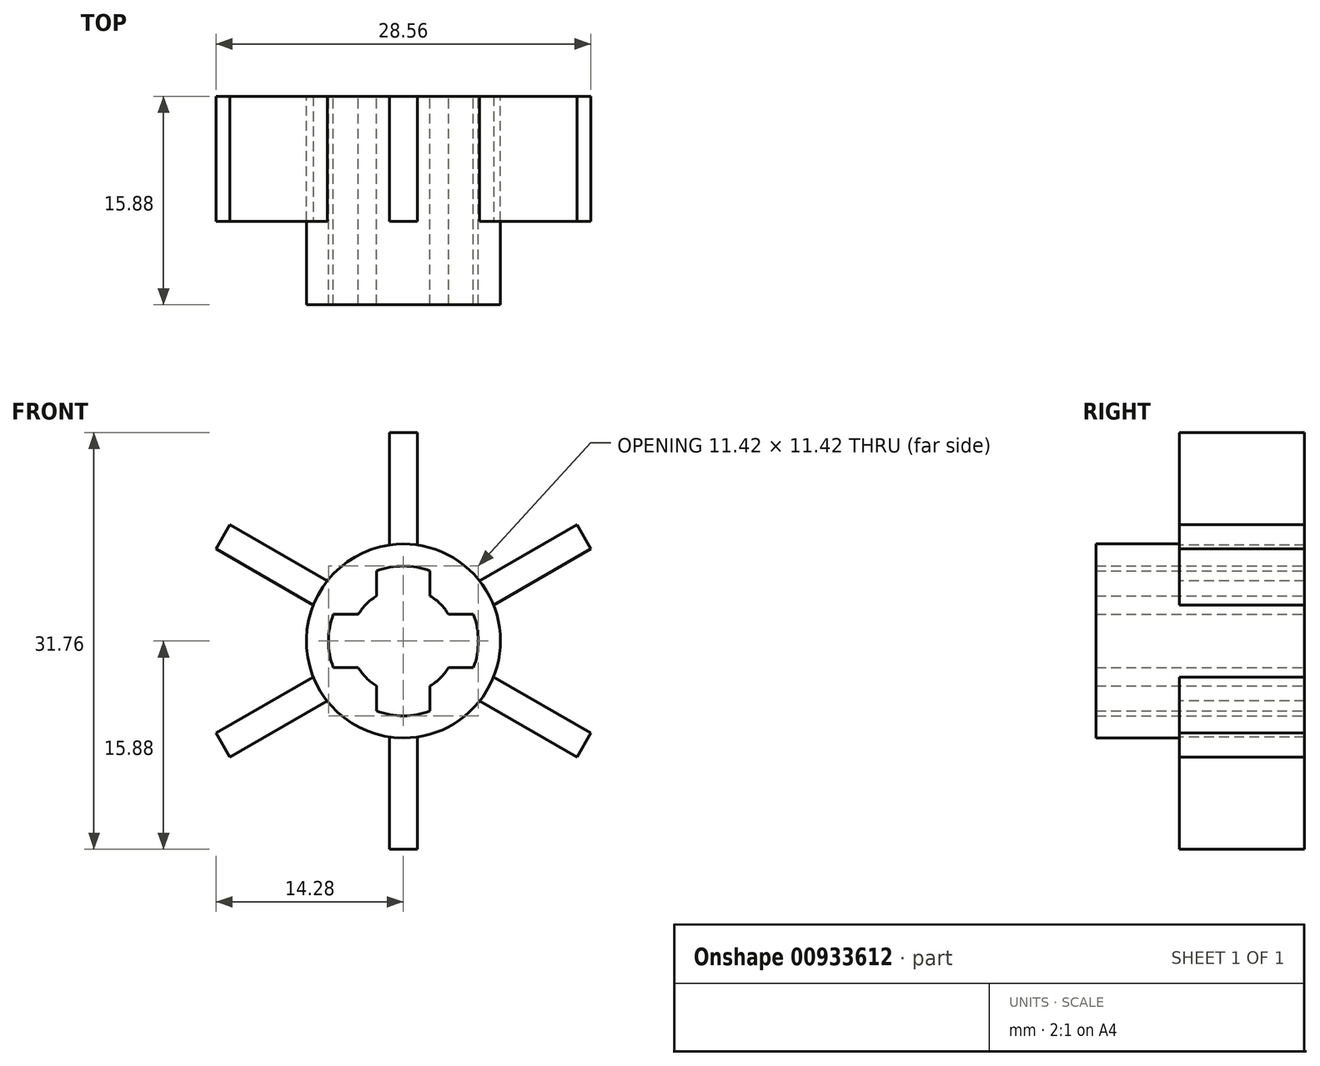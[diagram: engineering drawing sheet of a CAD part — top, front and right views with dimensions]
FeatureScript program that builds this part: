
annotation { "Feature Type Name" : "Feature", "Feature Type Description" : "" }
export const myFeature = defineFeature(function(context is Context, id is Id, definition is map)
    precondition{}
    {
        {
            var Q0;
            Q0=qCreatedBy(makeId("Front.planeOp"),FACE);
            var sketch = newSketch(context, id + "F0", { "sketchPlane" : qUnion([Q0])});
            skArc(sketch, "E0", {"start": v(-1.05, 6.26) * mm, "mid": v(-3.18, 5.5) * mm, "end": v(-4.9, 4.04) * mm});
            skCircle(sketch, "E1", {"center": v(0, 0) * mm, "radius": 3.99 * mm});
            skLineSegment(sketch, "E2.bottom", {"start": v(-1.05, 15.88) * mm, "end": v(1.05, 15.88) * mm});
            skLineSegment(sketch, "E2.top", {"start": v(-1.05, 6.26) * mm, "end": v(1.05, 6.26) * mm, "construction": true});
            skLineSegment(sketch, "E2.left", {"start": v(-1.05, 15.88) * mm, "end": v(-1.05, 6.26) * mm});
            skLineSegment(sketch, "E2.right", {"start": v(1.05, 15.88) * mm, "end": v(1.05, 6.26) * mm});
            skLineSegment(sketch, "E3", {"start": v(0, 0) * mm, "end": v(0, 6.26) * mm, "construction": true});
            skLineSegment(sketch, "E4", {"start": v(0, 0) * mm, "end": v(9.86, 0) * mm, "construction": true});
            skLineSegment(sketch, "E5.1.0", {"start": v(0, 0) * mm, "end": v(-5.42, 3.13) * mm, "construction": true});
            skLineSegment(sketch, "E5.1.1", {"start": v(-13.22, 8.85) * mm, "end": v(-4.9, 4.04) * mm});
            skLineSegment(sketch, "E5.1.2", {"start": v(-14.28, 7.02) * mm, "end": v(-13.22, 8.85) * mm});
            skLineSegment(sketch, "E5.1.3", {"start": v(-14.28, 7.02) * mm, "end": v(-5.95, 2.22) * mm});
            skLineSegment(sketch, "E5.2.0", {"start": v(0, 0) * mm, "end": v(-5.42, -3.13) * mm, "construction": true});
            skLineSegment(sketch, "E5.2.1", {"start": v(-14.28, -7.02) * mm, "end": v(-5.95, -2.22) * mm});
            skLineSegment(sketch, "E5.2.2", {"start": v(-13.22, -8.85) * mm, "end": v(-14.28, -7.02) * mm});
            skLineSegment(sketch, "E5.2.3", {"start": v(-13.22, -8.85) * mm, "end": v(-4.9, -4.04) * mm});
            skLineSegment(sketch, "E5.3.0", {"start": v(0, 0) * mm, "end": v(0, -6.26) * mm, "construction": true});
            skLineSegment(sketch, "E5.3.1", {"start": v(-1.05, -15.88) * mm, "end": v(-1.05, -6.26) * mm});
            skLineSegment(sketch, "E5.3.2", {"start": v(1.05, -15.88) * mm, "end": v(-1.05, -15.88) * mm});
            skLineSegment(sketch, "E5.3.3", {"start": v(1.05, -15.88) * mm, "end": v(1.05, -6.26) * mm});
            skLineSegment(sketch, "E5.4.0", {"start": v(0, 0) * mm, "end": v(5.42, -3.13) * mm, "construction": true});
            skLineSegment(sketch, "E5.4.1", {"start": v(13.22, -8.85) * mm, "end": v(4.9, -4.04) * mm});
            skLineSegment(sketch, "E5.4.2", {"start": v(14.28, -7.02) * mm, "end": v(13.22, -8.85) * mm});
            skLineSegment(sketch, "E5.4.3", {"start": v(14.28, -7.02) * mm, "end": v(5.95, -2.22) * mm});
            skLineSegment(sketch, "E5.5.0", {"start": v(0, 0) * mm, "end": v(5.42, 3.13) * mm, "construction": true});
            skLineSegment(sketch, "E5.5.1", {"start": v(14.28, 7.02) * mm, "end": v(5.95, 2.22) * mm});
            skLineSegment(sketch, "E5.5.2", {"start": v(13.22, 8.85) * mm, "end": v(14.28, 7.02) * mm});
            skLineSegment(sketch, "E5.5.3", {"start": v(13.22, 8.85) * mm, "end": v(4.9, 4.04) * mm});
            skArc(sketch, "E6.trimOffspring", {"start": v(4.9, 4.04) * mm, "mid": v(3.17, 5.5) * mm, "end": v(1.05, 6.26) * mm});
            skArc(sketch, "E7.trimOffspring", {"start": v(5.95, -2.22) * mm, "mid": v(6.35, 0) * mm, "end": v(5.95, 2.22) * mm});
            skArc(sketch, "E8.trimOffspring", {"start": v(1.05, -6.26) * mm, "mid": v(3.17, -5.5) * mm, "end": v(4.9, -4.04) * mm});
            skArc(sketch, "E9.trimOffspring", {"start": v(-4.9, -4.04) * mm, "mid": v(-3.18, -5.5) * mm, "end": v(-1.05, -6.26) * mm});
            skArc(sketch, "E10.trimOffspring", {"start": v(-5.95, 2.22) * mm, "mid": v(-6.35, 0) * mm, "end": v(-5.95, -2.22) * mm});
            skSolve(sketch);
        }
        {
            var Q0;
            Q0 = qSketchRegion(id + "F0", true);
            extrude(context, id + "F1", {"entities" : qUnion([Q0]), "depth" : 9.52 * mm, "offsetDistance" : 25.4 * mm});
        }
        {
            var Q0;
            Q0=makeQuery(id+"F1.opExtrude","CAP_FACE",FACE,{"disambiguationData":[OSD([sQuery(id+"F0.wireOp",EDGE,"E0"),sQuery(id+"F0.wireOp",EDGE,"E1"),sQuery(id+"F0.wireOp",EDGE,"E2.bottom"),sQuery(id+"F0.wireOp",EDGE,"E2.left"),sQuery(id+"F0.wireOp",EDGE,"E2.right"),sQuery(id+"F0.wireOp",EDGE,"E5.1.1"),sQuery(id+"F0.wireOp",EDGE,"E5.1.2"),sQuery(id+"F0.wireOp",EDGE,"E5.1.3"),sQuery(id+"F0.wireOp",EDGE,"E5.2.1"),sQuery(id+"F0.wireOp",EDGE,"E5.2.2"),sQuery(id+"F0.wireOp",EDGE,"E5.2.3"),sQuery(id+"F0.wireOp",EDGE,"E5.3.1"),sQuery(id+"F0.wireOp",EDGE,"E5.3.2"),sQuery(id+"F0.wireOp",EDGE,"E5.3.3"),sQuery(id+"F0.wireOp",EDGE,"E5.4.1"),sQuery(id+"F0.wireOp",EDGE,"E5.4.2"),sQuery(id+"F0.wireOp",EDGE,"E5.4.3"),sQuery(id+"F0.wireOp",EDGE,"E5.5.1"),sQuery(id+"F0.wireOp",EDGE,"E5.5.2"),sQuery(id+"F0.wireOp",EDGE,"E5.5.3"),sQuery(id+"F0.wireOp",EDGE,"E6.trimOffspring"),sQuery(id+"F0.wireOp",EDGE,"E7.trimOffspring"),sQuery(id+"F0.wireOp",EDGE,"E8.trimOffspring"),sQuery(id+"F0.wireOp",EDGE,"E9.trimOffspring"),sQuery(id+"F0.wireOp",EDGE,"E10.trimOffspring")])],"isStart":false});
            var sketch = newSketch(context, id + "F2", { "sketchPlane" : qUnion([Q0])});
            skCircle(sketch, "E11", {"center": v(0, 0) * mm, "radius": 7.4 * mm});
            skArc(sketch, "E12", {"start": v(-2.03, 3.43) * mm, "mid": v(-2.82, 2.82) * mm, "end": v(-3.43, 2.03) * mm});
            skLineSegment(sketch, "E13.bottom", {"start": v(-2.03, 5.33) * mm, "end": v(2.03, 5.33) * mm, "construction": true});
            skLineSegment(sketch, "E13.top", {"start": v(-2.03, 3.43) * mm, "end": v(2.03, 3.43) * mm, "construction": true});
            skLineSegment(sketch, "E13.left", {"start": v(-2.03, 5.33) * mm, "end": v(-2.03, 3.43) * mm});
            skLineSegment(sketch, "E13.right", {"start": v(2.03, 5.33) * mm, "end": v(2.03, 3.43) * mm});
            skLineSegment(sketch, "E14", {"start": v(0, 0) * mm, "end": v(0, 3.43) * mm, "construction": true});
            skPoint(sketch, "E14.endSnap0", {"position": v(0, 3.43) * mm});
            skLineSegment(sketch, "E15", {"start": v(0, 0) * mm, "end": v(1.34, 0) * mm, "construction": true});
            skArc(sketch, "E16", {"start": v(2.03, 5.33) * mm, "mid": v(0, 5.7) * mm, "end": v(-2.03, 5.33) * mm});
            skLineSegment(sketch, "E17.1.0", {"start": v(0, 0) * mm, "end": v(-3.43, 0) * mm, "construction": true});
            skLineSegment(sketch, "E17.1.1", {"start": v(-5.33, -2.03) * mm, "end": v(-3.43, -2.03) * mm});
            skArc(sketch, "E17.1.2", {"start": v(-5.33, 2.03) * mm, "mid": v(-5.7, 0) * mm, "end": v(-5.33, -2.03) * mm});
            skLineSegment(sketch, "E17.1.3", {"start": v(-5.33, 2.03) * mm, "end": v(-3.43, 2.03) * mm});
            skLineSegment(sketch, "E17.2.0", {"start": v(0, 0) * mm, "end": v(0, -3.43) * mm, "construction": true});
            skLineSegment(sketch, "E17.2.1", {"start": v(2.03, -5.33) * mm, "end": v(2.03, -3.43) * mm});
            skArc(sketch, "E17.2.2", {"start": v(-2.03, -5.33) * mm, "mid": v(0, -5.7) * mm, "end": v(2.03, -5.33) * mm});
            skLineSegment(sketch, "E17.2.3", {"start": v(-2.03, -5.33) * mm, "end": v(-2.03, -3.43) * mm});
            skLineSegment(sketch, "E17.3.0", {"start": v(0, 0) * mm, "end": v(3.43, 0) * mm, "construction": true});
            skLineSegment(sketch, "E17.3.1", {"start": v(5.33, 2.03) * mm, "end": v(3.43, 2.03) * mm});
            skArc(sketch, "E17.3.2", {"start": v(5.33, -2.03) * mm, "mid": v(5.7, 0) * mm, "end": v(5.33, 2.03) * mm});
            skLineSegment(sketch, "E17.3.3", {"start": v(5.33, -2.03) * mm, "end": v(3.43, -2.03) * mm});
            skArc(sketch, "E18.trimOffspring", {"start": v(-3.43, -2.03) * mm, "mid": v(-2.82, -2.82) * mm, "end": v(-2.03, -3.43) * mm});
            skArc(sketch, "E19.trimOffspring", {"start": v(3.43, 2.03) * mm, "mid": v(2.82, 2.82) * mm, "end": v(2.03, 3.43) * mm});
            skArc(sketch, "E20.trimOffspring", {"start": v(2.03, -3.43) * mm, "mid": v(2.82, -2.82) * mm, "end": v(3.43, -2.03) * mm});
            skSolve(sketch);
        }
        {
            var Q0;
            Q0 = qSketchRegion(id + "F2", true);
            extrude(context, id + "F3", {"entities" : qUnion([Q0]), "operationType" : NewBodyOperationType.ADD, "depth" : 6.35 * mm, "offsetDistance" : 25.4 * mm});
        }
        {
            var Q0;
            {var subQ0=sQuery(id+"F0.wireOp",EDGE,"E1");Q0=makeQuery(id+"F3.boolean.opBoolean","SPLIT",FACE,{"disambiguationData":[TD([makeQuery(id+"F3.opExtrude","SWEPT_FACE",FACE,{"disambiguationData":[OSD([sQuery(id+"F2.wireOp",EDGE,"E17.3.1")])]})])],"derivedFrom":makeQuery(id+"F1.opExtrude","CAP_FACE",FACE,{"disambiguationData":[OSD([sQuery(id+"F0.wireOp",EDGE,"E0"),subQ0,sQuery(id+"F0.wireOp",EDGE,"E2.bottom"),sQuery(id+"F0.wireOp",EDGE,"E2.left"),sQuery(id+"F0.wireOp",EDGE,"E2.right"),sQuery(id+"F0.wireOp",EDGE,"E5.1.1"),sQuery(id+"F0.wireOp",EDGE,"E5.1.2"),sQuery(id+"F0.wireOp",EDGE,"E5.1.3"),sQuery(id+"F0.wireOp",EDGE,"E5.2.1"),sQuery(id+"F0.wireOp",EDGE,"E5.2.2"),sQuery(id+"F0.wireOp",EDGE,"E5.2.3"),sQuery(id+"F0.wireOp",EDGE,"E5.3.1"),sQuery(id+"F0.wireOp",EDGE,"E5.3.2"),sQuery(id+"F0.wireOp",EDGE,"E5.3.3"),sQuery(id+"F0.wireOp",EDGE,"E5.4.1"),sQuery(id+"F0.wireOp",EDGE,"E5.4.2"),sQuery(id+"F0.wireOp",EDGE,"E5.4.3"),sQuery(id+"F0.wireOp",EDGE,"E5.5.1"),sQuery(id+"F0.wireOp",EDGE,"E5.5.2"),sQuery(id+"F0.wireOp",EDGE,"E5.5.3"),sQuery(id+"F0.wireOp",EDGE,"E6.trimOffspring"),sQuery(id+"F0.wireOp",EDGE,"E7.trimOffspring"),sQuery(id+"F0.wireOp",EDGE,"E8.trimOffspring"),sQuery(id+"F0.wireOp",EDGE,"E9.trimOffspring"),sQuery(id+"F0.wireOp",EDGE,"E10.trimOffspring")])],"isStart":false})});}
            var Q1;
            {var subQ0=sQuery(id+"F0.wireOp",EDGE,"E1");Q1=makeQuery(id+"F3.boolean.opBoolean","SPLIT",FACE,{"disambiguationData":[TD([makeQuery(id+"F3.opExtrude","SWEPT_FACE",FACE,{"disambiguationData":[OSD([sQuery(id+"F2.wireOp",EDGE,"E17.2.1")])]})])],"derivedFrom":makeQuery(id+"F1.opExtrude","CAP_FACE",FACE,{"disambiguationData":[OSD([sQuery(id+"F0.wireOp",EDGE,"E0"),subQ0,sQuery(id+"F0.wireOp",EDGE,"E2.bottom"),sQuery(id+"F0.wireOp",EDGE,"E2.left"),sQuery(id+"F0.wireOp",EDGE,"E2.right"),sQuery(id+"F0.wireOp",EDGE,"E5.1.1"),sQuery(id+"F0.wireOp",EDGE,"E5.1.2"),sQuery(id+"F0.wireOp",EDGE,"E5.1.3"),sQuery(id+"F0.wireOp",EDGE,"E5.2.1"),sQuery(id+"F0.wireOp",EDGE,"E5.2.2"),sQuery(id+"F0.wireOp",EDGE,"E5.2.3"),sQuery(id+"F0.wireOp",EDGE,"E5.3.1"),sQuery(id+"F0.wireOp",EDGE,"E5.3.2"),sQuery(id+"F0.wireOp",EDGE,"E5.3.3"),sQuery(id+"F0.wireOp",EDGE,"E5.4.1"),sQuery(id+"F0.wireOp",EDGE,"E5.4.2"),sQuery(id+"F0.wireOp",EDGE,"E5.4.3"),sQuery(id+"F0.wireOp",EDGE,"E5.5.1"),sQuery(id+"F0.wireOp",EDGE,"E5.5.2"),sQuery(id+"F0.wireOp",EDGE,"E5.5.3"),sQuery(id+"F0.wireOp",EDGE,"E6.trimOffspring"),sQuery(id+"F0.wireOp",EDGE,"E7.trimOffspring"),sQuery(id+"F0.wireOp",EDGE,"E8.trimOffspring"),sQuery(id+"F0.wireOp",EDGE,"E9.trimOffspring"),sQuery(id+"F0.wireOp",EDGE,"E10.trimOffspring")])],"isStart":false})});}
            var Q2;
            {var subQ0=sQuery(id+"F0.wireOp",EDGE,"E1");Q2=makeQuery(id+"F3.boolean.opBoolean","SPLIT",FACE,{"disambiguationData":[TD([makeQuery(id+"F3.opExtrude","SWEPT_FACE",FACE,{"disambiguationData":[OSD([sQuery(id+"F2.wireOp",EDGE,"E13.left")])]})])],"derivedFrom":makeQuery(id+"F1.opExtrude","CAP_FACE",FACE,{"disambiguationData":[OSD([sQuery(id+"F0.wireOp",EDGE,"E0"),subQ0,sQuery(id+"F0.wireOp",EDGE,"E2.bottom"),sQuery(id+"F0.wireOp",EDGE,"E2.left"),sQuery(id+"F0.wireOp",EDGE,"E2.right"),sQuery(id+"F0.wireOp",EDGE,"E5.1.1"),sQuery(id+"F0.wireOp",EDGE,"E5.1.2"),sQuery(id+"F0.wireOp",EDGE,"E5.1.3"),sQuery(id+"F0.wireOp",EDGE,"E5.2.1"),sQuery(id+"F0.wireOp",EDGE,"E5.2.2"),sQuery(id+"F0.wireOp",EDGE,"E5.2.3"),sQuery(id+"F0.wireOp",EDGE,"E5.3.1"),sQuery(id+"F0.wireOp",EDGE,"E5.3.2"),sQuery(id+"F0.wireOp",EDGE,"E5.3.3"),sQuery(id+"F0.wireOp",EDGE,"E5.4.1"),sQuery(id+"F0.wireOp",EDGE,"E5.4.2"),sQuery(id+"F0.wireOp",EDGE,"E5.4.3"),sQuery(id+"F0.wireOp",EDGE,"E5.5.1"),sQuery(id+"F0.wireOp",EDGE,"E5.5.2"),sQuery(id+"F0.wireOp",EDGE,"E5.5.3"),sQuery(id+"F0.wireOp",EDGE,"E6.trimOffspring"),sQuery(id+"F0.wireOp",EDGE,"E7.trimOffspring"),sQuery(id+"F0.wireOp",EDGE,"E8.trimOffspring"),sQuery(id+"F0.wireOp",EDGE,"E9.trimOffspring"),sQuery(id+"F0.wireOp",EDGE,"E10.trimOffspring")])],"isStart":false})});}
            var Q3;
            {var subQ0=sQuery(id+"F0.wireOp",EDGE,"E1");Q3=makeQuery(id+"F3.boolean.opBoolean","SPLIT",FACE,{"disambiguationData":[TD([makeQuery(id+"F3.opExtrude","SWEPT_FACE",FACE,{"disambiguationData":[OSD([sQuery(id+"F2.wireOp",EDGE,"E17.1.1")])]})])],"derivedFrom":makeQuery(id+"F1.opExtrude","CAP_FACE",FACE,{"disambiguationData":[OSD([sQuery(id+"F0.wireOp",EDGE,"E0"),subQ0,sQuery(id+"F0.wireOp",EDGE,"E2.bottom"),sQuery(id+"F0.wireOp",EDGE,"E2.left"),sQuery(id+"F0.wireOp",EDGE,"E2.right"),sQuery(id+"F0.wireOp",EDGE,"E5.1.1"),sQuery(id+"F0.wireOp",EDGE,"E5.1.2"),sQuery(id+"F0.wireOp",EDGE,"E5.1.3"),sQuery(id+"F0.wireOp",EDGE,"E5.2.1"),sQuery(id+"F0.wireOp",EDGE,"E5.2.2"),sQuery(id+"F0.wireOp",EDGE,"E5.2.3"),sQuery(id+"F0.wireOp",EDGE,"E5.3.1"),sQuery(id+"F0.wireOp",EDGE,"E5.3.2"),sQuery(id+"F0.wireOp",EDGE,"E5.3.3"),sQuery(id+"F0.wireOp",EDGE,"E5.4.1"),sQuery(id+"F0.wireOp",EDGE,"E5.4.2"),sQuery(id+"F0.wireOp",EDGE,"E5.4.3"),sQuery(id+"F0.wireOp",EDGE,"E5.5.1"),sQuery(id+"F0.wireOp",EDGE,"E5.5.2"),sQuery(id+"F0.wireOp",EDGE,"E5.5.3"),sQuery(id+"F0.wireOp",EDGE,"E6.trimOffspring"),sQuery(id+"F0.wireOp",EDGE,"E7.trimOffspring"),sQuery(id+"F0.wireOp",EDGE,"E8.trimOffspring"),sQuery(id+"F0.wireOp",EDGE,"E9.trimOffspring"),sQuery(id+"F0.wireOp",EDGE,"E10.trimOffspring")])],"isStart":false})});}
            extrude(context, id + "F4", {"entities" : qUnion([Q0, Q1, Q2, Q3]), "operationType" : NewBodyOperationType.REMOVE, "endBound" : BoundingType.THROUGH_ALL, "oppositeDirection" : true, "depth" : 7.94 * mm, "offsetDistance" : 25.4 * mm});
        }
        {
            var Q0;
            {var subQ2=sQuery(id+"F0.wireOp",EDGE,"E5.1.3");var subQ3=sQuery(id+"F2.wireOp",EDGE,"E11");Q0=makeQuery(id+"F3.boolean.opBoolean","SPLIT",FACE,{"disambiguationData":[TD([makeQuery(id+"F1.opExtrude","SWEPT_FACE",FACE,{"disambiguationData":[OSD([subQ2])]})])],"derivedFrom":makeQuery(id+"F3.opExtrude","CAP_FACE",FACE,{"disambiguationData":[OSD([subQ3,sQuery(id+"F2.wireOp",EDGE,"E12"),sQuery(id+"F2.wireOp",EDGE,"E13.left"),sQuery(id+"F2.wireOp",EDGE,"E13.right"),sQuery(id+"F2.wireOp",EDGE,"E16"),sQuery(id+"F2.wireOp",EDGE,"E17.1.1"),sQuery(id+"F2.wireOp",EDGE,"E17.1.2"),sQuery(id+"F2.wireOp",EDGE,"E17.1.3"),sQuery(id+"F2.wireOp",EDGE,"E17.2.1"),sQuery(id+"F2.wireOp",EDGE,"E17.2.2"),sQuery(id+"F2.wireOp",EDGE,"E17.2.3"),sQuery(id+"F2.wireOp",EDGE,"E17.3.1"),sQuery(id+"F2.wireOp",EDGE,"E17.3.2"),sQuery(id+"F2.wireOp",EDGE,"E17.3.3"),sQuery(id+"F2.wireOp",EDGE,"E18.trimOffspring"),sQuery(id+"F2.wireOp",EDGE,"E19.trimOffspring"),sQuery(id+"F2.wireOp",EDGE,"E20.trimOffspring")])],"isStart":true})});}
            var sketch = newSketch(context, id + "F5", { "sketchPlane" : qUnion([Q0])});
            skCircle(sketch, "E21", {"center": v(0, 0) * mm, "radius": 7.4 * mm});
            skCircle(sketch, "E22", {"center": v(0, 0) * mm, "radius": 6.35 * mm});
            skSolve(sketch);
        }
        {
            var Q0;
            Q0 = qSketchRegion(id + "F5", true);
            var Q1;
            Q1=makeQuery(id+"F1.opExtrude","CAP_FACE",FACE,{"disambiguationData":[OSD([sQuery(id+"F0.wireOp",EDGE,"E0"),sQuery(id+"F0.wireOp",EDGE,"E1"),sQuery(id+"F0.wireOp",EDGE,"E2.bottom"),sQuery(id+"F0.wireOp",EDGE,"E2.left"),sQuery(id+"F0.wireOp",EDGE,"E2.right"),sQuery(id+"F0.wireOp",EDGE,"E5.1.1"),sQuery(id+"F0.wireOp",EDGE,"E5.1.2"),sQuery(id+"F0.wireOp",EDGE,"E5.1.3"),sQuery(id+"F0.wireOp",EDGE,"E5.2.1"),sQuery(id+"F0.wireOp",EDGE,"E5.2.2"),sQuery(id+"F0.wireOp",EDGE,"E5.2.3"),sQuery(id+"F0.wireOp",EDGE,"E5.3.1"),sQuery(id+"F0.wireOp",EDGE,"E5.3.2"),sQuery(id+"F0.wireOp",EDGE,"E5.3.3"),sQuery(id+"F0.wireOp",EDGE,"E5.4.1"),sQuery(id+"F0.wireOp",EDGE,"E5.4.2"),sQuery(id+"F0.wireOp",EDGE,"E5.4.3"),sQuery(id+"F0.wireOp",EDGE,"E5.5.1"),sQuery(id+"F0.wireOp",EDGE,"E5.5.2"),sQuery(id+"F0.wireOp",EDGE,"E5.5.3"),sQuery(id+"F0.wireOp",EDGE,"E6.trimOffspring"),sQuery(id+"F0.wireOp",EDGE,"E7.trimOffspring"),sQuery(id+"F0.wireOp",EDGE,"E8.trimOffspring"),sQuery(id+"F0.wireOp",EDGE,"E9.trimOffspring"),sQuery(id+"F0.wireOp",EDGE,"E10.trimOffspring")])],"isStart":true});
            extrude(context, id + "F6", {"entities" : qUnion([Q0]), "operationType" : NewBodyOperationType.ADD, "endBound" : BoundingType.UP_TO_SURFACE, "depth" : 25.4 * mm, "endBoundEntityFace" : qUnion([Q1]), "offsetDistance" : 25.4 * mm});
        }
    });
